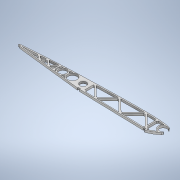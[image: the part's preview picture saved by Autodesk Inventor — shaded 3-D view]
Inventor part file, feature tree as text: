
AUTODESK INVENTOR PART (.ipt)
format: ipt  version: 2022 (Build 260153000, 153)  size: 448,000 bytes
history: native  units: mm
features: extrude x1, sketch x1
ambient origin geometry x8: Origin, YZ Plane, XZ Plane, XY Plane, X Axis, Y Axis, Z Axis, Center Point
bodies: Body1 (feature_tree)
feature tree (2):
  extrude  "Extrusion5"  Depth=10.0mm
  sketch  "Sketch1"  dims[d31=34.456mm d50=368.759386mm d57=16.0mm d69=8.0mm d70=23.0mm d71=8.0mm d73=16.0mm d80=19.0mm d81=16.0mm d82=1.0mm d83=1.0mm d84=1.0mm d85=1.0mm d86=1.0mm d87=0.8mm d88=1.0mm d90=19.0mm d94=5.0mm d95=5.0mm d105=5.0mm d106=5.0mm d108=2.0mm d109=19.0mm d114=5.0mm d115=5.0mm d116=24.0mm d117=2.5mm d118=2.5mm d123=2.5mm d124=2.5mm d125=10.0mm d126=24.0mm d127=24.0mm d128=27.0mm d135=0.5mm d136=45.0deg d139=7.0mm d165=45.0deg d169=27.0mm d175=90.0deg d181=45.0deg d185=7.0mm d186=45.0deg d190=7.0mm d191=45.0deg d197=90.0deg d203=90.0deg d206=7.0mm d207=5.0mm d208=0.0mm]
